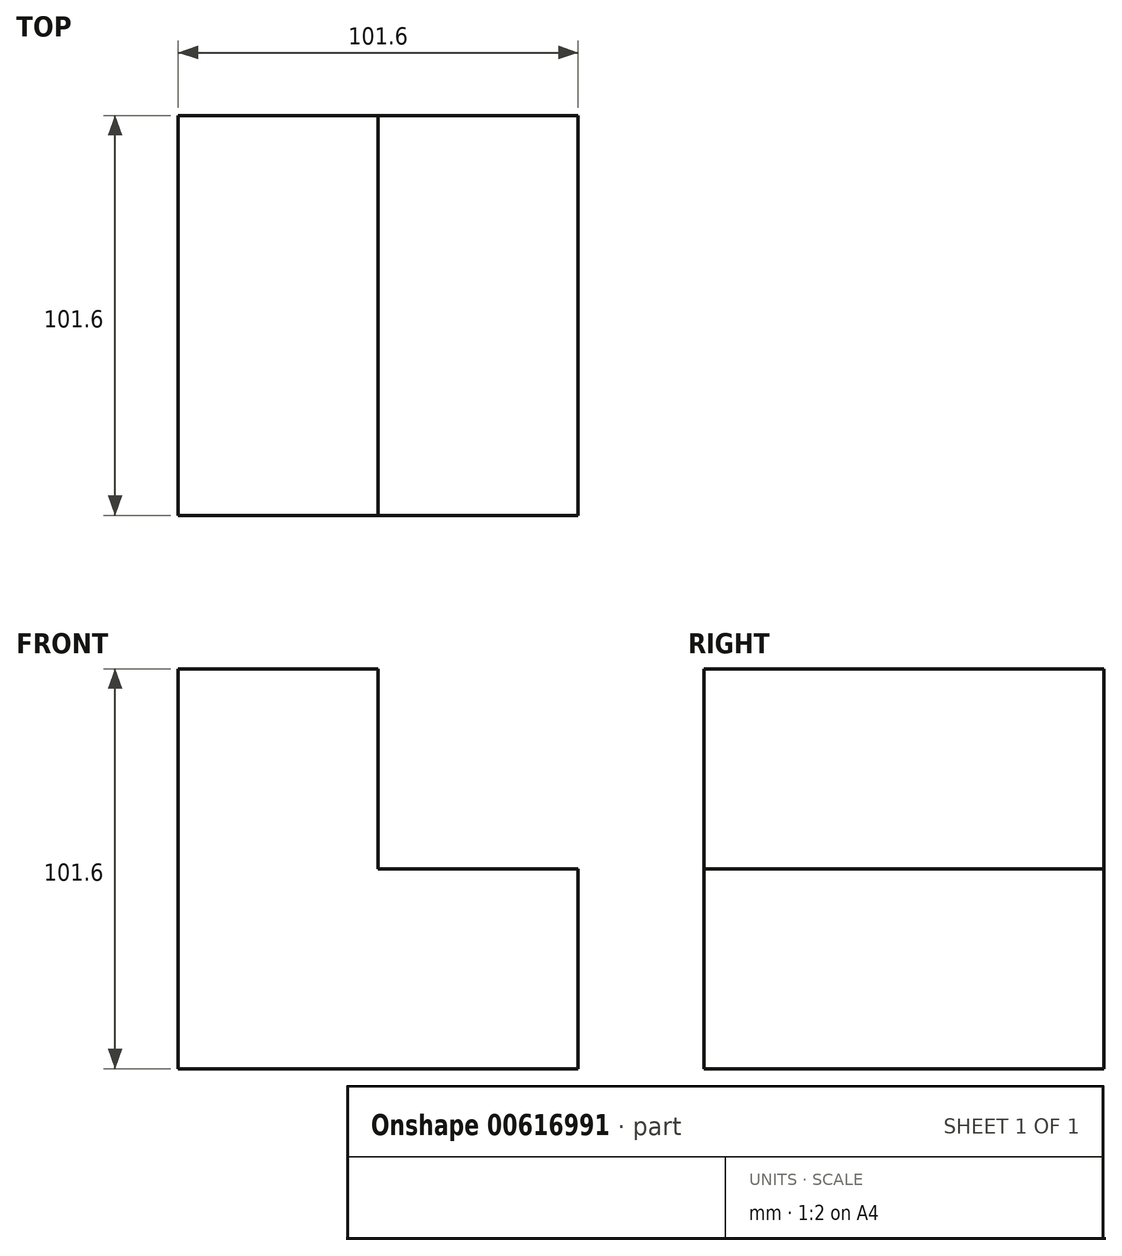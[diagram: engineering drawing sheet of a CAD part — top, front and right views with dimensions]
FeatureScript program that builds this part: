
annotation { "Feature Type Name" : "Feature", "Feature Type Description" : "" }
export const myFeature = defineFeature(function(context is Context, id is Id, definition is map)
    precondition{}
    {
        {
            var Q0;
            Q0=qCreatedBy(makeId("Front.planeOp"),FACE);
            var sketch = newSketch(context, id + "F0", { "sketchPlane" : qUnion([Q0])});
            skLineSegment(sketch, "E0.bottom", {"start": v(-52.23, -54.48) * mm, "end": v(-1.43, -54.48) * mm});
            skLineSegment(sketch, "E0.top", {"start": v(-52.23, 47.12) * mm, "end": v(-1.43, 47.12) * mm});
            skLineSegment(sketch, "E0.left", {"start": v(-52.23, -54.48) * mm, "end": v(-52.23, 47.12) * mm});
            skLineSegment(sketch, "E0.right", {"start": v(-1.43, -54.48) * mm, "end": v(-1.43, 47.12) * mm});
            skPoint(sketch, "E0.middle", {"position": v(-26.83, -3.68) * mm});
            skLineSegment(sketch, "E1", {"start": v(-1.43, -54.48) * mm, "end": v(49.37, -54.48) * mm});
            skLineSegment(sketch, "E2", {"start": v(49.37, -54.48) * mm, "end": v(49.37, -3.68) * mm});
            skPoint(sketch, "E2.endSnap0", {"position": v(-1.43, -3.68) * mm});
            skLineSegment(sketch, "E3", {"start": v(49.37, -3.68) * mm, "end": v(-1.43, -3.68) * mm});
            skSolve(sketch);
        }
        {
            var Q0;
            Q0 = qSketchRegion(id + "F0", true);
            extrude(context, id + "F1", {"entities" : qUnion([Q0]), "endBound" : BoundingType.SYMMETRIC, "depth" : 101.6 * mm, "offsetDistance" : 25.4 * mm});
        }
    });
